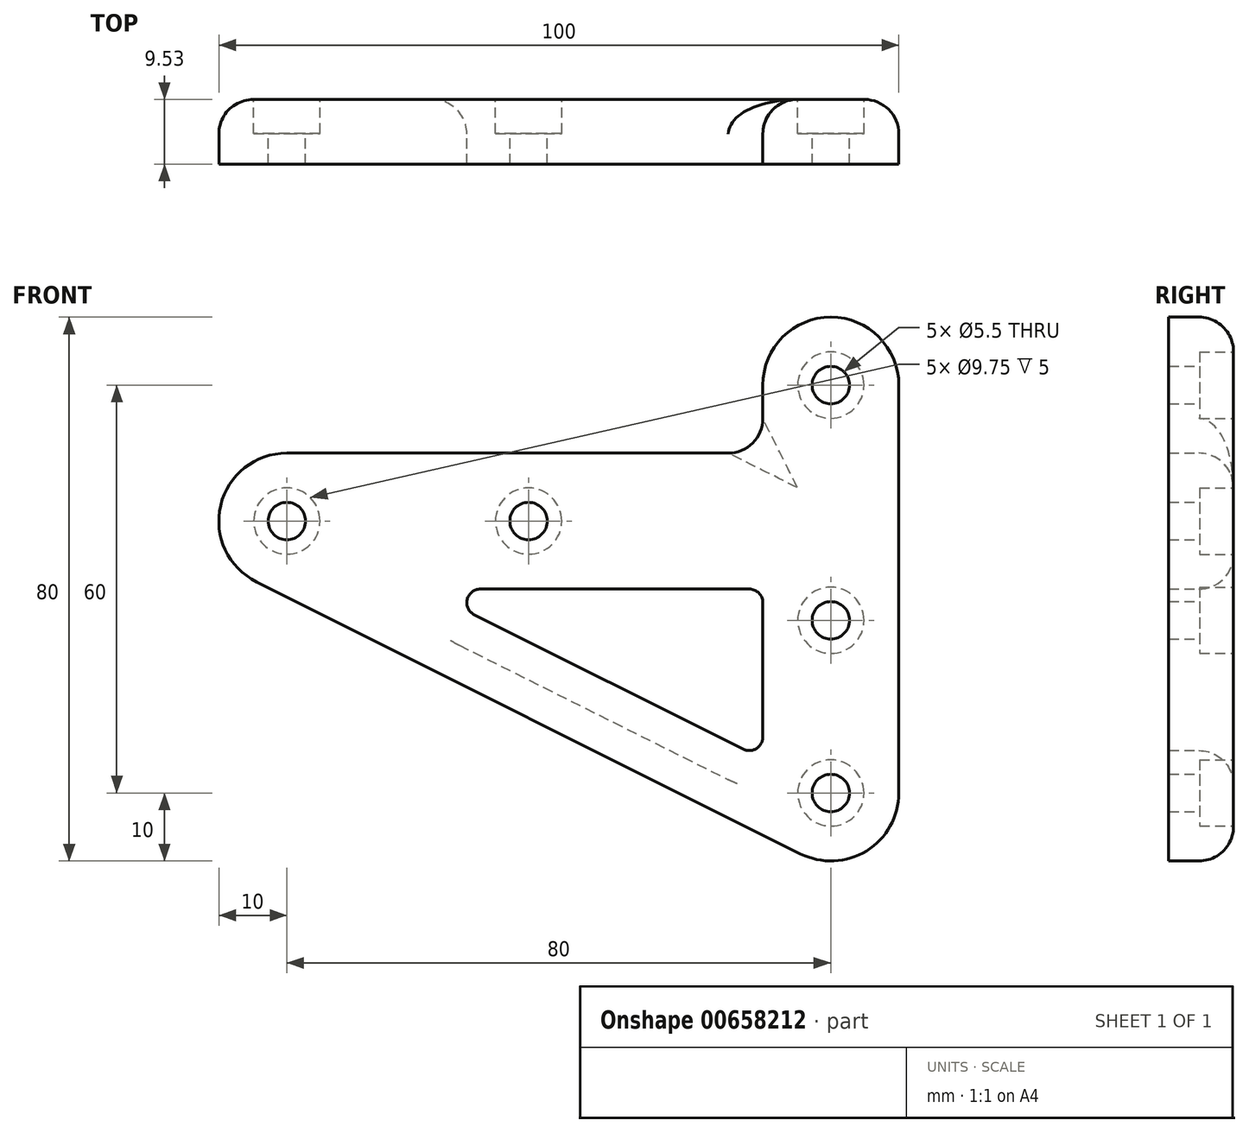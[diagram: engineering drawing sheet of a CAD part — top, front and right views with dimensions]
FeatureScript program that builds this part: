
annotation { "Feature Type Name" : "Feature", "Feature Type Description" : "" }
export const myFeature = defineFeature(function(context is Context, id is Id, definition is map)
    precondition{}
    {
        {
            var Q0;
            Q0=qCreatedBy(makeId("Front.planeOp"),FACE);
            var sketch = newSketch(context, id + "F0", { "sketchPlane" : qUnion([Q0])});
            skPoint(sketch, "E0.MirrorP", {"position": v(-44.45, 0) * mm});
            skPoint(sketch, "E1", {"position": v(0, -40) * mm});
            skArc(sketch, "E2", {"start": v(-4.47, -48.94) * mm, "mid": v(5.26, -48.5) * mm, "end": v(10, -40) * mm});
            skArc(sketch, "E3", {"start": v(-80, 10) * mm, "mid": v(-89.73, 2.3) * mm, "end": v(-84.47, -8.94) * mm});
            skPoint(sketch, "E4", {"position": v(0, 0) * mm});
            skLineSegment(sketch, "E5", {"start": v(-84.47, -8.94) * mm, "end": v(-4.47, -48.94) * mm});
            skLineSegment(sketch, "E6", {"start": v(-80, 10) * mm, "end": v(-10, 10) * mm});
            skLineSegment(sketch, "E7", {"start": v(10, -40) * mm, "end": v(10, 0) * mm});
            skLineSegment(sketch, "E8.0", {"start": v(-52.42, -13.79) * mm, "end": v(-12.9, -33.55) * mm});
            skLineSegment(sketch, "E9.0", {"start": v(-10, -31.76) * mm, "end": v(-10, -12) * mm});
            skLineSegment(sketch, "E10.0", {"start": v(-51.53, -10) * mm, "end": v(-12, -10) * mm});
            skPoint(sketch, "E11.visualSharp", {"position": v(-60, -10) * mm});
            skArc(sketch, "E11.filletArc", {"start": v(-51.53, -10) * mm, "mid": v(-53.47, -11.54) * mm, "end": v(-52.42, -13.79) * mm});
            skPoint(sketch, "E12.visualSharp", {"position": v(-10, -10) * mm});
            skArc(sketch, "E12.filletArc", {"start": v(-10, -12) * mm, "mid": v(-10.59, -10.59) * mm, "end": v(-12, -10) * mm});
            skPoint(sketch, "E13.visualSharp", {"position": v(-10, -35) * mm});
            skArc(sketch, "E13.filletArc", {"start": v(-12.9, -33.55) * mm, "mid": v(-10.95, -33.47) * mm, "end": v(-10, -31.76) * mm});
            skPoint(sketch, "E14", {"position": v(0, 20) * mm});
            skArc(sketch, "E15", {"start": v(10, 20) * mm, "mid": v(0, 30) * mm, "end": v(-10, 20) * mm});
            skLineSegment(sketch, "E16", {"start": v(10, 0) * mm, "end": v(10, 20) * mm});
            skLineSegment(sketch, "E17", {"start": v(-10, 20) * mm, "end": v(-10, 10) * mm});
            skPoint(sketch, "E18.orphan", {"position": v(0, 10) * mm});
            skPoint(sketch, "E19", {"position": v(0, -14.6) * mm});
            skSolve(sketch);
        }
        {
            var Q0;
            Q0=makeQuery(id+"F0.imprint","IMPRINT",FACE,{"disambiguationData":[TD([[makeQuery(id+"F0.imprint","IMPRINT",EDGE,{"derivedFrom":sQuery(id+"F0.wireOp",EDGE,"E2")}),1.0]])]});
            extrude(context, id + "F1", {"entities" : qUnion([Q0]), "depth" : 9.52 * mm, "offsetDistance" : 25.4 * mm});
        }
        {
            var Q0;
            Q0=sQuery(id+"F0.wireOp",VERTEX,"E14");
            var Q1;
            Q1=sQuery(id+"F0.wireOp",VERTEX,"E0.MirrorP");
            var Q2;
            Q2=sQuery(id+"F0.wireOp",VERTEX,"E3.center");
            var Q3;
            Q3=sQuery(id+"F0.wireOp",VERTEX,"E1");
            var Q4;
            Q4=sQuery(id+"F0.wireOp",VERTEX,"E19");
            var Q5;
            Q5=makeQuery(id+"F1.opExtrude","SWEPT_BODY",BODY,{"disambiguationData":[OSD([sQuery(id+"F0.wireOp",EDGE,"E2"),sQuery(id+"F0.wireOp",EDGE,"E3"),sQuery(id+"F0.wireOp",EDGE,"E5"),sQuery(id+"F0.wireOp",EDGE,"E6"),sQuery(id+"F0.wireOp",EDGE,"E7"),sQuery(id+"F0.wireOp",EDGE,"E8.0"),sQuery(id+"F0.wireOp",EDGE,"E9.0"),sQuery(id+"F0.wireOp",EDGE,"E10.0"),sQuery(id+"F0.wireOp",EDGE,"E11.filletArc"),sQuery(id+"F0.wireOp",EDGE,"E12.filletArc"),sQuery(id+"F0.wireOp",EDGE,"E13.filletArc"),sQuery(id+"F0.wireOp",EDGE,"E15"),sQuery(id+"F0.wireOp",EDGE,"E16"),sQuery(id+"F0.wireOp",EDGE,"E17")])]});
            hole(context, id + "F2", {"style" : HoleStyle.C_BORE, "endStyle" : HoleEndStyle.THROUGH, "oppositeDirection" : true, "standardTappedOrClearance" : lookupTablePath({ "standard" : "ISO", "fit" : "Normal", "size" : "M5", "type" : "Clearance" }), "standardBlindInLast" : lookupTablePath({ "fit" : "Standard", "standard" : "ISO", "size" : "M5", "type" : "Clearance" }), "holeDiameter" : 5.5 * mm, "cBoreDiameter" : 9.75 * mm, "cBoreDepth" : 5 * mm, "majorDiameter" : 6.35 * mm, "isTappedThrough" : true, "tappedDepth" : 12.7 * mm, "tapClearance" : 3, "locations" : qUnion([Q0, Q1, Q2, Q3, Q4]), "scope" : qUnion([Q5])});
        }
        {
            var Q0;
            Q0=makeQuery(id+"F1.opExtrude","CAP_EDGE",EDGE,{"disambiguationData":[OSD([sQuery(id+"F0.wireOp",EDGE,"E6")])],"isStart":true});
            var Q1;
            Q1=makeQuery(id+"F1.opExtrude","CAP_EDGE",EDGE,{"disambiguationData":[OSD([sQuery(id+"F0.wireOp",EDGE,"E10.0")])],"isStart":true});
            fillet(context, id + "F3", {"entities" : qUnion([Q0, Q1]), "radius" : 5.08 * mm, "tangentPropagation" : true, "allowEdgeOverflow" : false});
        }
        {
            var Q0;
            Q0=makeQuery(id+"F1.opExtrude","SWEPT_EDGE",EDGE,{"disambiguationData":[OSD([sQuery(id+"F0.wireOp",EDGE,"E6"),sQuery(id+"F0.wireOp",EDGE,"E17")])]});
            fillet(context, id + "F4", {"entities" : qUnion([Q0]), "radius" : 5.08 * mm, "tangentPropagation" : true, "allowEdgeOverflow" : false});
        }
    });
